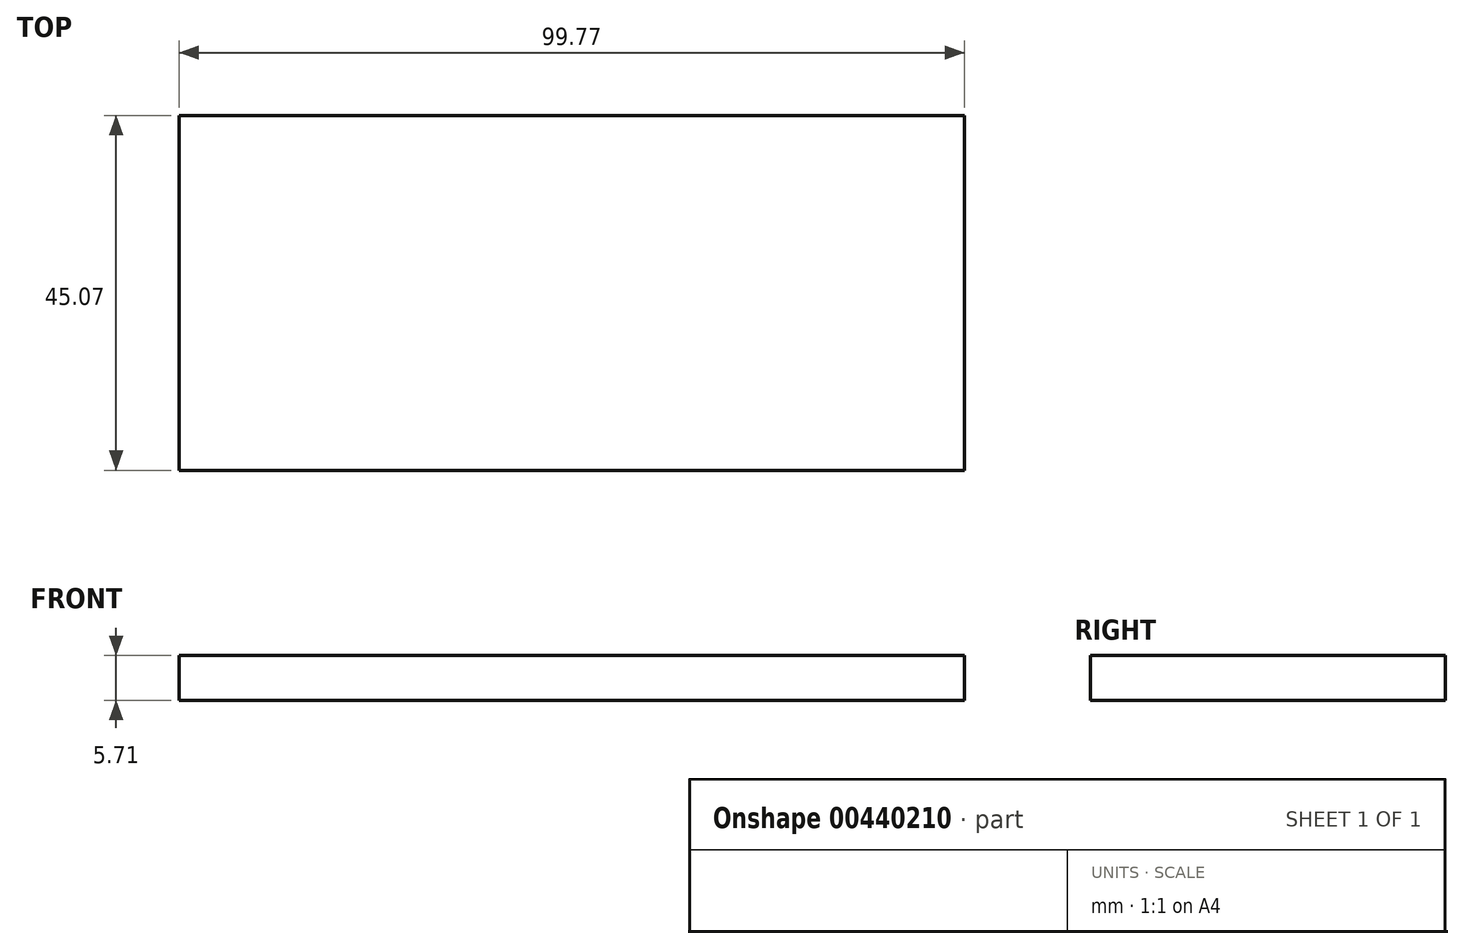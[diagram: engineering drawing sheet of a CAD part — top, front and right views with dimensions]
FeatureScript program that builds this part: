
annotation { "Feature Type Name" : "Feature", "Feature Type Description" : "" }
export const myFeature = defineFeature(function(context is Context, id is Id, definition is map)
    precondition{}
    {
        {
            var Q0;
            Q0=qCreatedBy(makeId("Top.planeOp"),FACE);
            var sketch = newSketch(context, id + "F0", { "sketchPlane" : qUnion([Q0])});
            skLineSegment(sketch, "E0", {"start": v(-59.77, -29.16) * mm, "end": v(-59.77, 15.9) * mm});
            skLineSegment(sketch, "E1", {"start": v(-59.77, 15.9) * mm, "end": v(40, 15.9) * mm});
            skLineSegment(sketch, "E2", {"start": v(40, 15.9) * mm, "end": v(40, -29.16) * mm});
            skLineSegment(sketch, "E3", {"start": v(40, -29.16) * mm, "end": v(-59.77, -29.16) * mm});
            skSolve(sketch);
        }
        {
            var Q0;
            Q0 = qSketchRegion(id + "F0", true);
            extrude(context, id + "F1", {"entities" : qUnion([Q0]), "depth" : 5.7 * mm});
        }
    });
